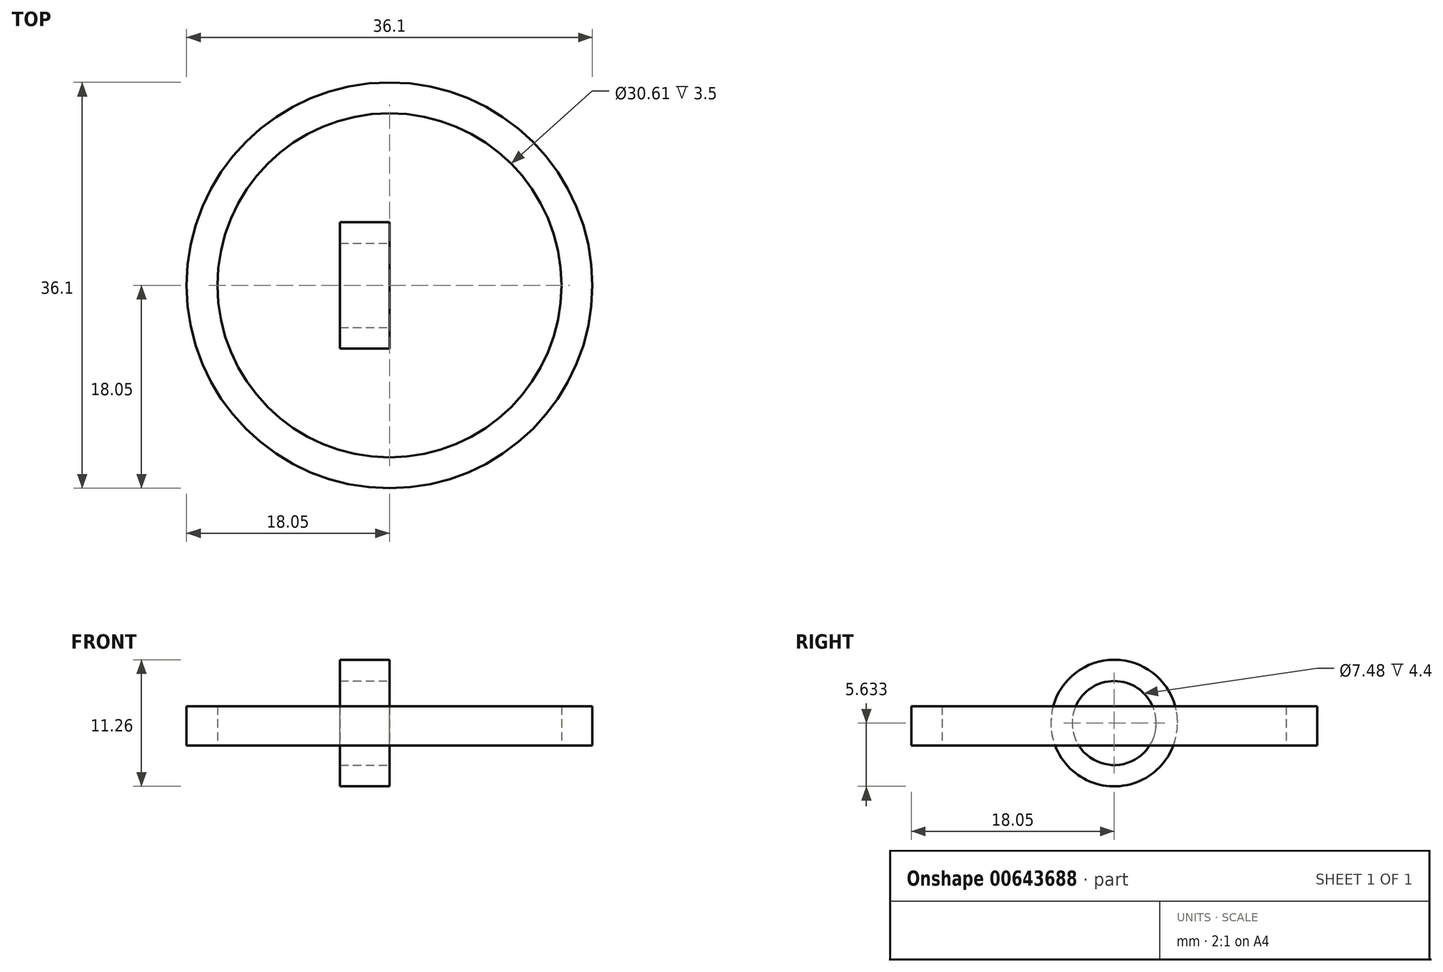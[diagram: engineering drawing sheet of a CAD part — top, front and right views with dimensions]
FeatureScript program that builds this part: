
annotation { "Feature Type Name" : "Feature", "Feature Type Description" : "" }
export const myFeature = defineFeature(function(context is Context, id is Id, definition is map)
    precondition{}
    {
        {
            var Q0;
            Q0=qCreatedBy(makeId("Top.planeOp"),FACE);
            var sketch = newSketch(context, id + "F0", { "sketchPlane" : qUnion([Q0])});
            skCircle(sketch, "E0", {"center": v(0, 0) * mm, "radius": 18.05 * mm});
            skCircle(sketch, "E1", {"center": v(0, 0) * mm, "radius": 15.3 * mm});
            skSolve(sketch);
        }
        {
            var Q0;
            Q0 = qSketchRegion(id + "F0", true);
            extrude(context, id + "F1", {"entities" : qUnion([Q0]), "depth" : 3.5 * mm, "offsetDistance" : 25 * mm});
        }
        {
            var Q0;
            Q0=qCreatedBy(makeId("Right.planeOp"),FACE);
            var sketch = newSketch(context, id + "F2", { "sketchPlane" : qUnion([Q0])});
            skCircle(sketch, "E2", {"center": v(0, 2.01) * mm, "radius": 5.63 * mm});
            skCircle(sketch, "E3", {"center": v(0, 2.01) * mm, "radius": 3.74 * mm});
            skSolve(sketch);
        }
        {
            var Q0;
            Q0 = qSketchRegion(id + "F2", true);
            extrude(context, id + "F3", {"entities" : qUnion([Q0]), "oppositeDirection" : true, "depth" : 4.4 * mm, "offsetDistance" : 25 * mm});
        }
        {
            var Q0;
            Q0=makeQuery(id+"F3.opExtrude","SWEPT_BODY",BODY,{"disambiguationData":[OSD([sQuery(id+"F2.wireOp",EDGE,"E2"),sQuery(id+"F2.wireOp",EDGE,"E3")])]});
            var Q1;
            Q1=makeQuery(id+"F3.opExtrude","CAP_EDGE",EDGE,{"disambiguationData":[OSD([sQuery(id+"F2.wireOp",EDGE,"E2")])],"isStart":true});
            transform(context, id + "F4", {"entities" : qUnion([Q0]), "transformType" : TransformType.ROTATION, "transformAxis" : qUnion([Q1]), "angle" : 30 * degree, "makeCopy" : false});
        }
    });
